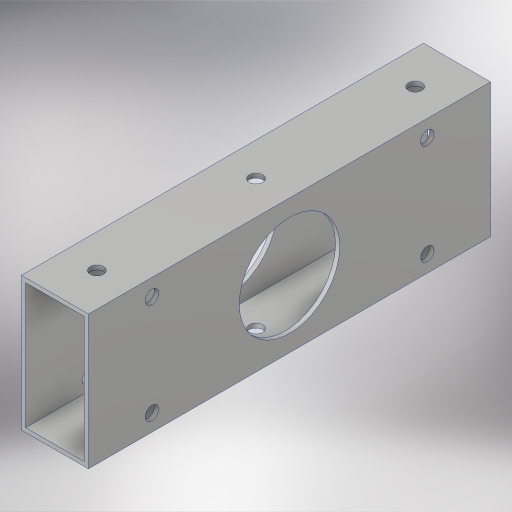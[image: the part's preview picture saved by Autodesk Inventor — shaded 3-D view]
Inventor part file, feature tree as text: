
AUTODESK INVENTOR PART (.ipt)
format: ipt  version: 2023.4 (Build 274418000, 418)  size: 320,000 bytes
history: native  units: in
note: dims shown in document units (in); Inventor stores cm internally (conversion verified against a paired STEP export)
features: sketch x4, hole x3, extrude x2, projected_geometry x1
ambient origin geometry x8: Origin, YZ Plane, XZ Plane, XY Plane, X Axis, Y Axis, Z Axis, Center Point
bodies: Solid1 (feature_tree)
feature tree (10):
  extrude  "Extrusion1"  Depth=4.75in
  hole  "Hole1"  [1 undecoded]
  hole  "Hole3"  [1 undecoded]
  extrude  "Extrusion2"  Depth=1.0in
  hole  "Hole2"  [1 undecoded]
  sketch  "Sketch2"  dims[d4=0.0in d5=4.75in]
  projected_geometry  "Projected Loop1"
  sketch  "Sketch3"  dims[d6=0.201in d7=0.75in d8=0.385in d9=0.25in d10=0.5635in d11=1.0in d12=0.8108in d14=4.7244in]
  sketch  "Sketch4"  dims[d15=3.7402in d16=4.2323in]
  sketch  "Sketch5"  dims[d17=1.5in d18=0.156in d19=0.38in d20=0.375in d21=0.25in d22=0.5635in d23=1.0in d24=0.8108in d28=1.5in d29=0.201in d30=0.38in d31=0.385in d32=0.25in d33=0.5635in d34=1.0in d35=0.8108in d36=1.5in d37=1.0in d38=0.0in d39=4.1098in]
note: 3 required parameter values undecoded (feature->parameter linkage not recoverable at this tier; creation-order binding heuristic only, values carry confidence <= 0.55)
